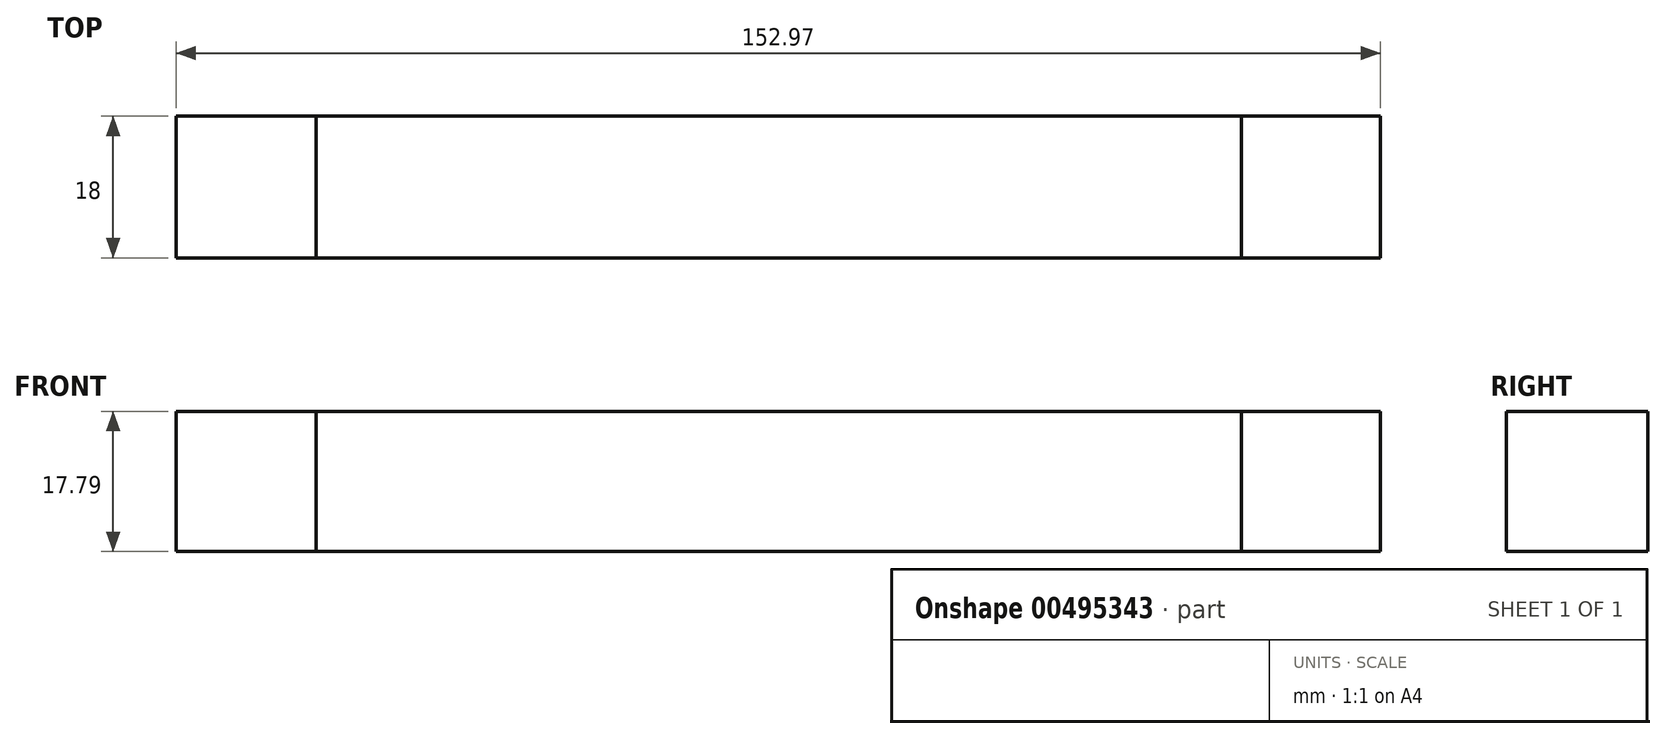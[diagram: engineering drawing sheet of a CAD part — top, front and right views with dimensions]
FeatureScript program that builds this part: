
annotation { "Feature Type Name" : "Feature", "Feature Type Description" : "" }
export const myFeature = defineFeature(function(context is Context, id is Id, definition is map)
    precondition{}
    {
        {
            var Q0;
            Q0=qCreatedBy(makeId("Front.planeOp"),FACE);
            var sketch = newSketch(context, id + "F0", { "sketchPlane" : qUnion([Q0])});
            skLineSegment(sketch, "E0.bottom", {"start": v(0, 0) * mm, "end": v(17.79, 0) * mm});
            skLineSegment(sketch, "E0.top", {"start": v(0, 17.79) * mm, "end": v(17.79, 17.79) * mm});
            skLineSegment(sketch, "E0.left", {"start": v(0, 0) * mm, "end": v(0, 17.79) * mm});
            skLineSegment(sketch, "E0.right", {"start": v(17.79, 0) * mm, "end": v(17.79, 17.79) * mm});
            skLineSegment(sketch, "E1.bottom", {"start": v(17.79, 0) * mm, "end": v(135.35, 0) * mm});
            skLineSegment(sketch, "E1.top", {"start": v(17.79, 17.79) * mm, "end": v(135.35, 17.79) * mm});
            skLineSegment(sketch, "E1.right", {"start": v(135.35, 0) * mm, "end": v(135.35, 17.79) * mm});
            skLineSegment(sketch, "E2.bottom", {"start": v(135.35, 0) * mm, "end": v(152.97, 0) * mm});
            skLineSegment(sketch, "E2.top", {"start": v(135.35, 17.79) * mm, "end": v(152.97, 17.79) * mm});
            skLineSegment(sketch, "E2.right", {"start": v(152.97, 0) * mm, "end": v(152.97, 17.79) * mm});
            skSolve(sketch);
        }
        {
            var Q0;
            Q0=makeQuery(id+"F0.imprint","IMPRINT",FACE,{"disambiguationData":[TD([[makeQuery(id+"F0.imprint","IMPRINT",EDGE,{"derivedFrom":sQuery(id+"F0.wireOp",EDGE,"E0.bottom")}),1.0]])]});
            var Q1;
            Q1=makeQuery(id+"F0.imprint","IMPRINT",FACE,{"disambiguationData":[TD([[makeQuery(id+"F0.imprint","IMPRINT",EDGE,{"derivedFrom":sQuery(id+"F0.wireOp",EDGE,"E2.bottom")}),1.0]])]});
            extrude(context, id + "F1", {"entities" : qUnion([Q0, Q1]), "depth" : 18 * mm});
        }
        {
            var Q0;
            Q0=makeQuery(id+"F0.imprint","IMPRINT",FACE,{"disambiguationData":[TD([[makeQuery(id+"F0.imprint","IMPRINT",EDGE,{"derivedFrom":sQuery(id+"F0.wireOp",EDGE,"E1.bottom")}),1.0]])]});
            extrude(context, id + "F2", {"entities" : qUnion([Q0]), "depth" : 18 * mm});
        }
    });
